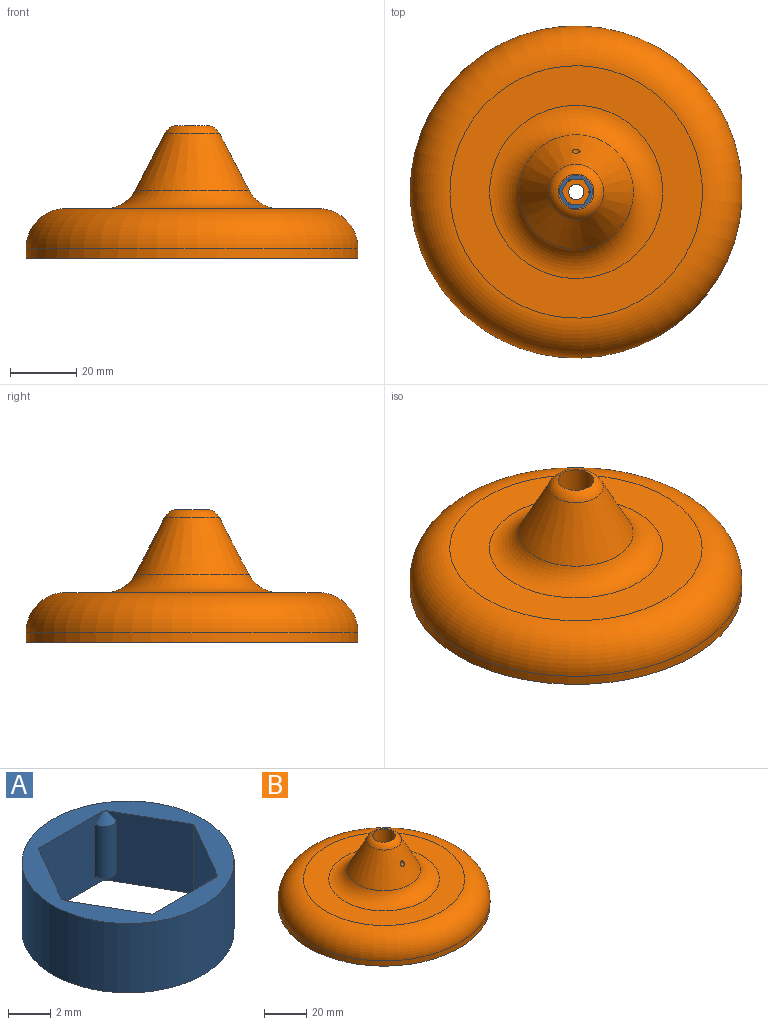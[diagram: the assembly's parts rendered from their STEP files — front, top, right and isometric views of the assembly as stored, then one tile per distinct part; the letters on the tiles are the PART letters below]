
ASSEMBLY  parts=2 mates=1
PART A: 18 faces, bbox 10x10x4 mm
  f0: plane 4x3.71mm, normal (0.87,-0.5,0), area 15.4mm2, adj f1,f7,f8,f12,f13,f14
  f1: plane 4.29x4mm, normal (0,-1,0), area 15.4mm2, adj f0,f7,f8,f9,f10,f11
  f2: plane 4x3.71mm, normal (-0.87,-0.5,0), area 15.4mm2, adj f3,f7,f8,f9,f10,f11
  f3: plane 4x3.71mm, normal (-0.87,0.5,0), area 15.4mm2, adj f2,f7,f8,f15,f16,f17
  f4: plane 4.29x4mm, normal (0,1,0), area 15.4mm2, adj f5,f7,f8,f15,f16,f17
  f5: plane 4x3.71mm, normal (0.87,0.5,0), area 15.4mm2, adj f4,f7,f8,f12,f13,f14
  f6: cylinder r=5mm len=10mm, axis (0,0,-1), area 125.7mm2, adj f7,f8
  f7: plane 10x10mm, normal (0,0,1), area 28.5mm2, adj f0,f1,f2,f3,f4,f5,f6,f10
  f8: plane 10x10mm, normal (0,0,-1), area 28.5mm2, adj f0,f1,f2,f3,f4,f5,f6,f11
  f9: cylinder r=0.6mm len=3mm, axis (0,0,-1), area 3.8mm2, adj f1,f2,f10,f11
  f10: cone r=0.1mm half-angle=45deg, axis (0,0,-1), area 0.5mm2, adj f1,f2,f7,f9
  f11: cone r=0.6mm half-angle=45deg, axis (0,0,1), area 0.5mm2, adj f1,f2,f8,f9
  f12: cylinder r=0.6mm len=3mm, axis (0,0,-1), area 3.8mm2, adj f0,f5,f13,f14
  f13: cone r=0.1mm half-angle=45deg, axis (0,0,-1), area 0.5mm2, adj f0,f5,f7,f12
  f14: cone r=0.6mm half-angle=45deg, axis (0,0,1), area 0.5mm2, adj f0,f5,f8,f12
  f15: cylinder r=0.6mm len=3mm, axis (0,0,-1), area 3.8mm2, adj f3,f4,f16,f17
  f16: cone r=0.1mm half-angle=45deg, axis (0,0,-1), area 0.5mm2, adj f3,f4,f7,f15
  f17: cone r=0.6mm half-angle=45deg, axis (0,0,1), area 0.5mm2, adj f3,f4,f8,f15
PART B: 15 faces, bbox 108.2x108.2x40 mm
  f0: cone r=20mm half-angle=27.5deg, axis (0,0,-1), area 1542.4mm2, adj f10,f12,f13
  f1: cylinder r=5.35mm len=21mm, axis (0,0,1), area 701.3mm2, adj f6,f10,f12
  f2: cylinder r=50mm len=100mm, axis (0,0,-1), area 942.5mm2, adj f4,f14
  f3: plane 76x76mm, normal (0,0,1), area 2401.1mm2, adj f13,f14
  f4: plane 100x100mm, normal (0,0,-1), area 2312.2mm2, adj f2,f11
  f5: plane 84x84mm, normal (0,0,-1), area 5525.2mm2, adj f9,f11
  f6: plane 10.7x10.7mm, normal (0,0,1), area 11.4mm2, adj f1,f7
  f7: cylinder r=5mm len=10mm, axis (0,0,1), area 125.7mm2, adj f6,f8
  f8: plane 10x10mm, normal (0,0,1), area 61.9mm2, adj f7,f9
  f9: cylinder r=2.3mm len=4.6mm, axis (0,0,1), area 28.9mm2, adj f5,f8
  f10: cylinder r=1.2mm len=7.61mm, axis (0,1,0), area 51.9mm2, adj f0,f1
  f11: cylinder r=42mm len=84mm, axis (0,0,1), area 3430.6mm2, adj f4,f5
  f12: torus R=3.84mm, axis (0,0,1), area 172.1mm2, adj f0,f1
  f13: torus R=26.07mm, axis (0,0,1), area 1449.2mm2, adj f0,f3
  f14: torus R=38mm, axis (0,0,1), area 5405.3mm2, adj f2,f3
PLACE A rot(axis=(0,-1,0),180deg) t=(0,0,19)mm
PLACE B rot(axis=(0,0,1),180deg) t=(0,0,0)mm
MATE fastened B.f1 <-> A.f6  axis (0,0,1) through (0,0,15)mm
